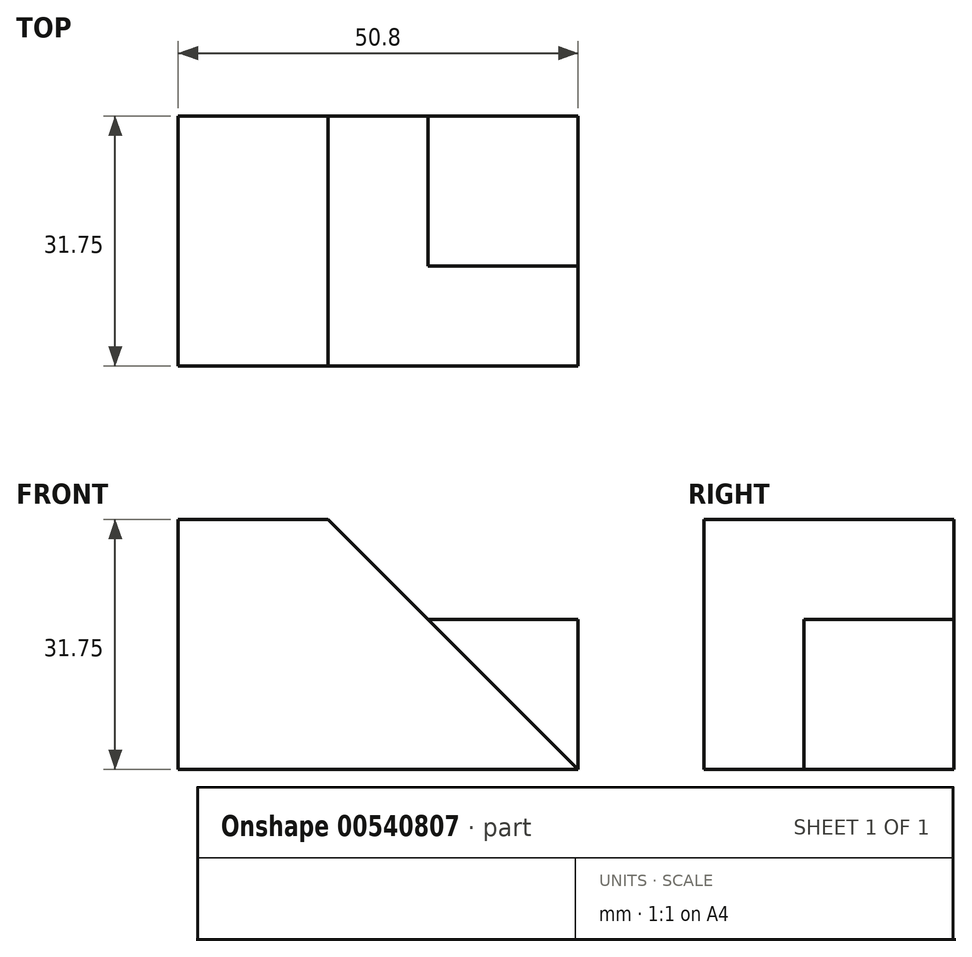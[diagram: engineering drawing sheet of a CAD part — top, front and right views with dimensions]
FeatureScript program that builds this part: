
annotation { "Feature Type Name" : "Feature", "Feature Type Description" : "" }
export const myFeature = defineFeature(function(context is Context, id is Id, definition is map)
    precondition{}
    {
        {
            var Q0;
            Q0=qCreatedBy(makeId("Front.planeOp"),FACE);
            var sketch = newSketch(context, id + "F0", { "sketchPlane" : qUnion([Q0])});
            skLineSegment(sketch, "E0", {"start": v(0, 0) * mm, "end": v(50.8, 0) * mm});
            skLineSegment(sketch, "E1", {"start": v(50.8, 0) * mm, "end": v(50.8, 31.75) * mm});
            skLineSegment(sketch, "E2", {"start": v(50.8, 31.75) * mm, "end": v(0, 31.75) * mm});
            skLineSegment(sketch, "E3", {"start": v(0, 31.75) * mm, "end": v(0, 0) * mm});
            skSolve(sketch);
        }
        {
            var Q0;
            Q0=makeQuery(id+"F0.imprint","IMPRINT",FACE,{"disambiguationData":[TD([[makeQuery(id+"F0.imprint","IMPRINT",EDGE,{"derivedFrom":sQuery(id+"F0.wireOp",EDGE,"E0")}),1.0]])]});
            extrude(context, id + "F1", {"entities" : qUnion([Q0]), "depth" : 31.75 * mm, "offsetDistance" : 25.4 * mm});
        }
        {
            var Q0;
            Q0=makeQuery(id+"F1.opExtrude","CAP_FACE",FACE,{"disambiguationData":[OSD([sQuery(id+"F0.wireOp",EDGE,"E0"),sQuery(id+"F0.wireOp",EDGE,"E1"),sQuery(id+"F0.wireOp",EDGE,"E2"),sQuery(id+"F0.wireOp",EDGE,"E3")])],"isStart":false});
            var sketch = newSketch(context, id + "F2", { "sketchPlane" : qUnion([Q0])});
            skLineSegment(sketch, "E4", {"start": v(50.8, 0) * mm, "end": v(19.05, 31.75) * mm});
            skLineSegment(sketch, "E5", {"start": v(19.05, 31.75) * mm, "end": v(50.8, 31.75) * mm});
            skLineSegment(sketch, "E6", {"start": v(50.8, 31.75) * mm, "end": v(50.8, 0) * mm});
            skSolve(sketch);
        }
        {
            var Q0;
            Q0=makeQuery(id+"F2.imprint","IMPRINT",FACE,{"disambiguationData":[TD([[makeQuery(id+"F2.imprint","IMPRINT",EDGE,{"derivedFrom":sQuery(id+"F2.wireOp",EDGE,"E4")}),-1.0]])]});
            extrude(context, id + "F3", {"entities" : qUnion([Q0]), "operationType" : NewBodyOperationType.REMOVE, "oppositeDirection" : true, "depth" : 12.7 * mm, "offsetDistance" : 25.4 * mm});
        }
        {
            var Q0;
            Q0=makeQuery(id+"F3.boolean.opBoolean","COPY",FACE,{"derivedFrom":makeQuery(id+"F3.opExtrude","CAP_FACE",FACE,{"disambiguationData":[OSD([sQuery(id+"F2.wireOp",EDGE,"E4"),sQuery(id+"F2.wireOp",EDGE,"E5"),sQuery(id+"F2.wireOp",EDGE,"E6")])],"isStart":false})});
            var sketch = newSketch(context, id + "F4", { "sketchPlane" : qUnion([Q0])});
            skLineSegment(sketch, "E7", {"start": v(31.75, 19.05) * mm, "end": v(31.75, 31.75) * mm});
            skLineSegment(sketch, "E8", {"start": v(31.75, 31.75) * mm, "end": v(19.05, 31.75) * mm});
            skLineSegment(sketch, "E9", {"start": v(19.05, 31.75) * mm, "end": v(31.75, 19.05) * mm});
            skSolve(sketch);
        }
        {
            var Q0;
            Q0=makeQuery(id+"F4.imprint","IMPRINT",FACE,{"disambiguationData":[TD([[makeQuery(id+"F4.imprint","IMPRINT",EDGE,{"derivedFrom":sQuery(id+"F4.wireOp",EDGE,"E7")}),1.0]])]});
            extrude(context, id + "F5", {"entities" : qUnion([Q0]), "operationType" : NewBodyOperationType.REMOVE, "oppositeDirection" : true, "depth" : 19.05 * mm, "offsetDistance" : 25.4 * mm});
        }
        {
            var Q0;
            Q0=makeQuery(id+"F1.opExtrude","CAP_FACE",FACE,{"disambiguationData":[OSD([sQuery(id+"F0.wireOp",EDGE,"E0"),sQuery(id+"F0.wireOp",EDGE,"E1"),sQuery(id+"F0.wireOp",EDGE,"E2"),sQuery(id+"F0.wireOp",EDGE,"E3")])],"isStart":true});
            var sketch = newSketch(context, id + "F6", { "sketchPlane" : qUnion([Q0])});
            skLineSegment(sketch, "E10", {"start": v(-31.75, 19.05) * mm, "end": v(-50.8, 19.05) * mm});
            skLineSegment(sketch, "E11", {"start": v(-50.8, 19.05) * mm, "end": v(-50.8, 31.75) * mm});
            skLineSegment(sketch, "E12", {"start": v(-50.8, 31.75) * mm, "end": v(-31.75, 31.75) * mm});
            skLineSegment(sketch, "E13", {"start": v(-31.75, 31.75) * mm, "end": v(-31.75, 19.05) * mm});
            skSolve(sketch);
        }
        {
            var Q0;
            Q0=makeQuery(id+"F6.imprint","IMPRINT",FACE,{"disambiguationData":[TD([[makeQuery(id+"F6.imprint","IMPRINT",EDGE,{"derivedFrom":sQuery(id+"F6.wireOp",EDGE,"E10")}),-1.0]])]});
            extrude(context, id + "F7", {"entities" : qUnion([Q0]), "operationType" : NewBodyOperationType.REMOVE, "oppositeDirection" : true, "depth" : 19.05 * mm, "offsetDistance" : 25.4 * mm});
        }
    });
